# Revit family: 63_LF_UN_Signify Trueline Suspended L1410 POE_IVLB
name_source: partatom
category: Lighting Fixtures
revit_build: Autodesk Revit 2017 (Build: 20190508_0315(x64)
units: mm (PartAtom-declared; Revit-internal decimal feet)

## family parameters
Always vertical = No
Cut with Voids When Loaded = No
Light Source = No
Part Type = Normal
Room Calculation Point = No
Round Connector Dimension = Use Diameter
Shared = No
Work Plane-Based = No

## types (1)
- Costumizable ll Family Instance
    Apparent Load = 0 VA
    Assembly Code = 63.0
    Description = Geometry copy of fixture
    Family Instance = EURS_63_LF_FB_TrueLine suspended SP530P SP531P SP532P SP533P L1410 POE_PHI : SP530P L1410 1 xLED19S_830 OC
    IfcExportAs = IfcLightFixtureType
    IfcExportType = USERDEFINED
    Model = Generic Geometry
    Rotation XZ Axis = 0.00°
    Rotation YZ Axis = 0.00°
    Type Comments = Unhosted - IVLibrary

## geometry (parser evidence)
native form markers: Blend x14, Sweep x25
no freeform markers — native parametric forms only
